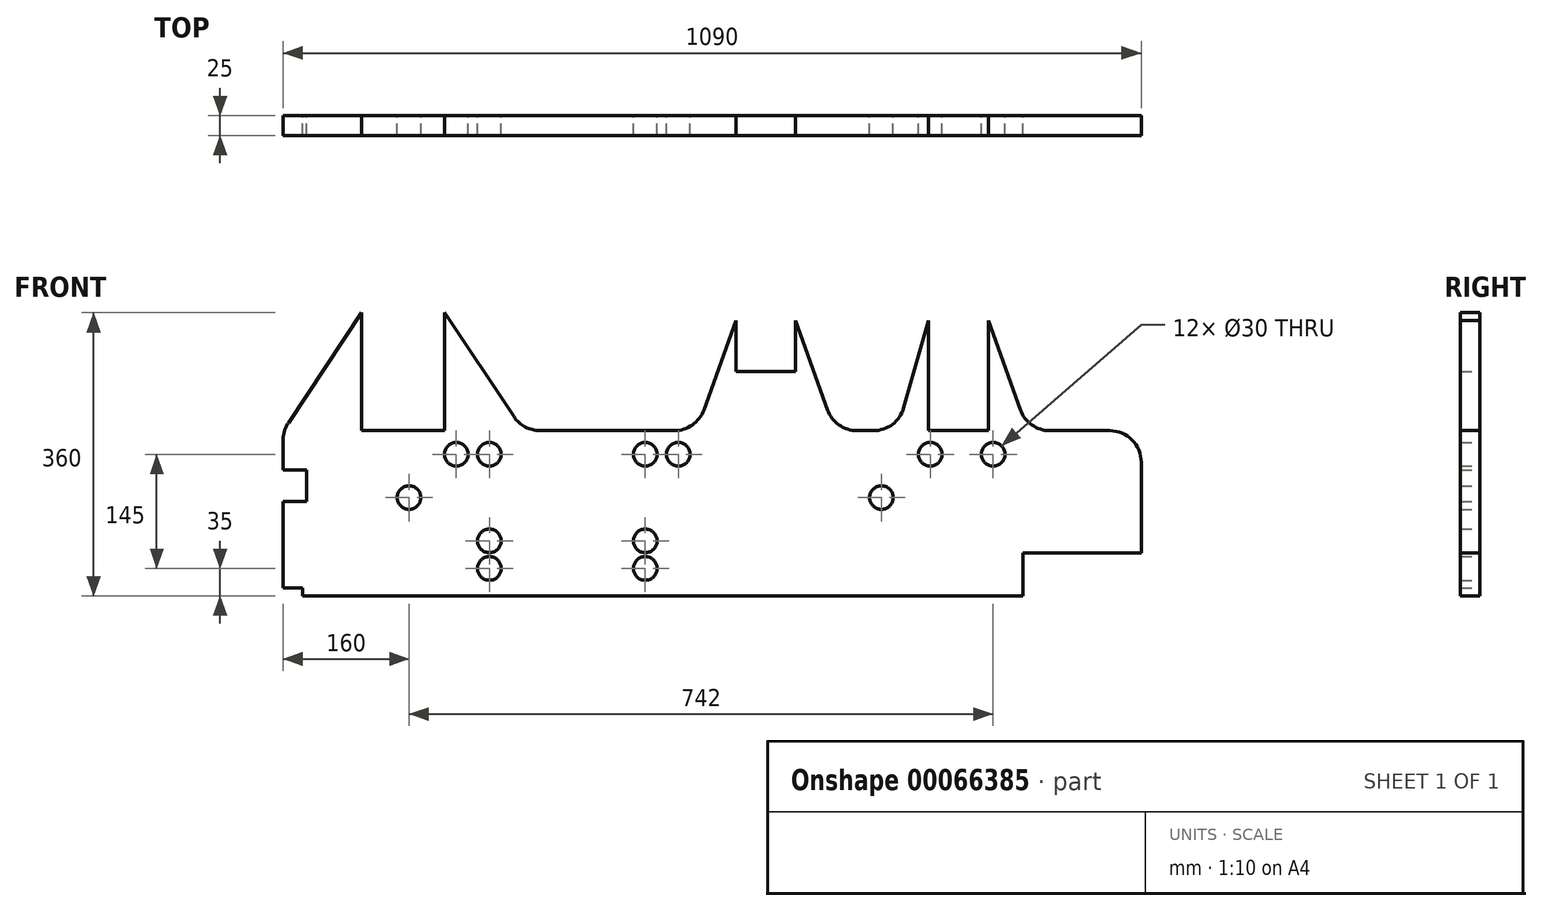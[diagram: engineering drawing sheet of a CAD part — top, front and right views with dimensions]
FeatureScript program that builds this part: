
annotation { "Feature Type Name" : "Feature", "Feature Type Description" : "" }
export const myFeature = defineFeature(function(context is Context, id is Id, definition is map)
    precondition{}
    {
        {
            var Q0;
            Q0=qCreatedBy(makeId("Front.planeOp"),FACE);
            var sketch = newSketch(context, id + "F0", { "sketchPlane" : qUnion([Q0])});
            skLineSegment(sketch, "E0", {"start": v(6.72, 10.08) * mm, "end": v(100, 150) * mm});
            skLineSegment(sketch, "E1", {"start": v(100, 150) * mm, "end": v(100, 0) * mm});
            skLineSegment(sketch, "E2", {"start": v(100, 0) * mm, "end": v(205, 0) * mm});
            skLineSegment(sketch, "E3", {"start": v(205, 0) * mm, "end": v(205, 150) * mm});
            skLineSegment(sketch, "E4", {"start": v(205, 150) * mm, "end": v(293.13, 17.81) * mm});
            skLineSegment(sketch, "E5", {"start": v(326.4, 0) * mm, "end": v(496.81, 0) * mm});
            skLineSegment(sketch, "E6", {"start": v(534.48, 26.55) * mm, "end": v(575, 140) * mm});
            skLineSegment(sketch, "E7", {"start": v(575, 140) * mm, "end": v(575, 75) * mm});
            skLineSegment(sketch, "E8", {"start": v(575, 75) * mm, "end": v(651, 75) * mm});
            skLineSegment(sketch, "E9", {"start": v(651, 75) * mm, "end": v(651, 140) * mm});
            skLineSegment(sketch, "E10", {"start": v(651, 140) * mm, "end": v(691.52, 26.55) * mm});
            skLineSegment(sketch, "E11", {"start": v(729.19, 0) * mm, "end": v(749.83, 0) * mm});
            skLineSegment(sketch, "E12", {"start": v(788.29, 29.01) * mm, "end": v(820, 140) * mm});
            skLineSegment(sketch, "E13", {"start": v(820, 140) * mm, "end": v(820, 0) * mm});
            skLineSegment(sketch, "E14", {"start": v(820, 0) * mm, "end": v(896, 0) * mm});
            skLineSegment(sketch, "E15", {"start": v(896, 0) * mm, "end": v(896, 140) * mm});
            skLineSegment(sketch, "E16", {"start": v(896, 140) * mm, "end": v(936.52, 26.55) * mm});
            skLineSegment(sketch, "E17", {"start": v(974.19, 0) * mm, "end": v(1050, 0) * mm});
            skLineSegment(sketch, "E18", {"start": v(1090, -40) * mm, "end": v(1090, -170) * mm});
            skLineSegment(sketch, "E19", {"start": v(1050, -210) * mm, "end": v(0, -210) * mm});
            skLineSegment(sketch, "E20", {"start": v(0, -210) * mm, "end": v(0, -12.11) * mm});
            skLineSegment(sketch, "E21", {"start": v(0, -200) * mm, "end": v(25, -200) * mm});
            skLineSegment(sketch, "E22", {"start": v(25, -200) * mm, "end": v(25, -210) * mm});
            skCircle(sketch, "E23", {"center": v(220, -30) * mm, "radius": 15 * mm});
            skCircle(sketch, "E24", {"center": v(262, -30) * mm, "radius": 15 * mm});
            skCircle(sketch, "E25", {"center": v(460, -30) * mm, "radius": 15 * mm});
            skCircle(sketch, "E26", {"center": v(502, -30) * mm, "radius": 15 * mm});
            skCircle(sketch, "E27", {"center": v(460, -140) * mm, "radius": 15 * mm});
            skCircle(sketch, "E28", {"center": v(460, -175) * mm, "radius": 15 * mm});
            skCircle(sketch, "E29", {"center": v(262, -140) * mm, "radius": 15 * mm});
            skCircle(sketch, "E30", {"center": v(262, -175) * mm, "radius": 15 * mm});
            skPoint(sketch, "E31.visualSharp", {"position": v(305, 0) * mm});
            skArc(sketch, "E31.filletArc", {"start": v(293.13, 17.81) * mm, "mid": v(307.53, 4.73) * mm, "end": v(326.4, 0) * mm});
            skPoint(sketch, "E32.visualSharp", {"position": v(525, 0) * mm});
            skArc(sketch, "E32.filletArc", {"start": v(496.81, 0) * mm, "mid": v(519.85, 7.3) * mm, "end": v(534.48, 26.55) * mm});
            skPoint(sketch, "E33.visualSharp", {"position": v(701, 0) * mm});
            skArc(sketch, "E33.filletArc", {"start": v(691.52, 26.55) * mm, "mid": v(706.15, 7.3) * mm, "end": v(729.19, 0) * mm});
            skPoint(sketch, "E34.visualSharp", {"position": v(780, 0) * mm});
            skArc(sketch, "E34.filletArc", {"start": v(749.83, 0) * mm, "mid": v(773.92, 8.07) * mm, "end": v(788.29, 29.01) * mm});
            skPoint(sketch, "E35.visualSharp", {"position": v(946, 0) * mm});
            skArc(sketch, "E35.filletArc", {"start": v(936.52, 26.55) * mm, "mid": v(951.15, 7.3) * mm, "end": v(974.19, 0) * mm});
            skPoint(sketch, "E36.visualSharp", {"position": v(1090, 0) * mm});
            skArc(sketch, "E36.filletArc", {"start": v(1090, -40) * mm, "mid": v(1078.28, -11.72) * mm, "end": v(1050, 0) * mm});
            skPoint(sketch, "E37.visualSharp", {"position": v(1090, -210) * mm});
            skArc(sketch, "E37.filletArc", {"start": v(1050, -210) * mm, "mid": v(1078.28, -198.28) * mm, "end": v(1090, -170) * mm});
            skPoint(sketch, "E38.visualSharp", {"position": v(0, 0) * mm});
            skArc(sketch, "E38.filletArc", {"start": v(6.72, 10.08) * mm, "mid": v(1.72, -0.52) * mm, "end": v(0, -12.11) * mm});
            skLineSegment(sketch, "E39.bottom", {"start": v(0, -50) * mm, "end": v(30, -50) * mm});
            skLineSegment(sketch, "E39.top", {"start": v(0, -90) * mm, "end": v(30, -90) * mm});
            skLineSegment(sketch, "E39.left", {"start": v(0, -50) * mm, "end": v(0, -90) * mm});
            skLineSegment(sketch, "E39.right", {"start": v(30, -50) * mm, "end": v(30, -90) * mm});
            skLineSegment(sketch, "E40.bottom", {"start": v(1090, -155) * mm, "end": v(940, -155) * mm});
            skLineSegment(sketch, "E40.top", {"start": v(1090, -210) * mm, "end": v(940, -210) * mm});
            skLineSegment(sketch, "E40.left", {"start": v(1090, -155) * mm, "end": v(1090, -210) * mm});
            skLineSegment(sketch, "E40.right", {"start": v(940, -155) * mm, "end": v(940, -210) * mm});
            skCircle(sketch, "E41", {"center": v(902, -30) * mm, "radius": 15 * mm});
            skCircle(sketch, "E42", {"center": v(822, -30) * mm, "radius": 15 * mm});
            skCircle(sketch, "E43", {"center": v(760, -85) * mm, "radius": 15 * mm});
            skCircle(sketch, "E44", {"center": v(160, -85) * mm, "radius": 15 * mm});
            skPoint(sketch, "E44.centerSnap0", {"position": v(0, -70) * mm});
            skSolve(sketch);
        }
        {
            var Q0;
            Q0=makeQuery(id+"F0.imprint","IMPRINT",FACE,{"disambiguationData":[TD([[makeQuery(id+"F0.imprint","IMPRINT",EDGE,{"derivedFrom":sQuery(id+"F0.wireOp",EDGE,"E0")}),-1.0]])]});
            extrude(context, id + "F1", {"entities" : qUnion([Q0]), "depth" : 25 * mm});
        }
    });
